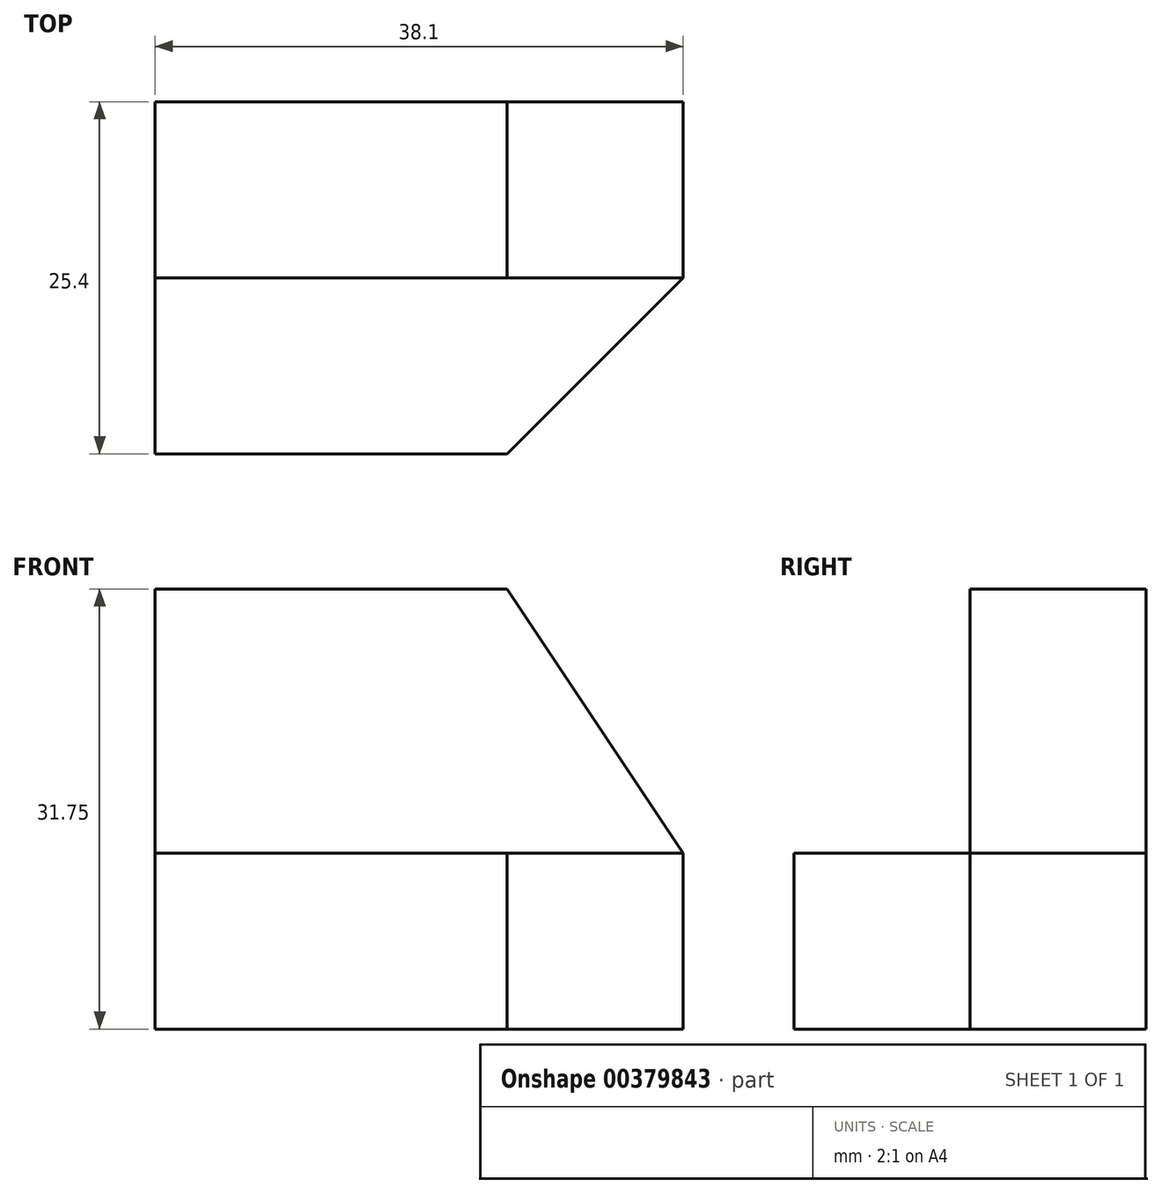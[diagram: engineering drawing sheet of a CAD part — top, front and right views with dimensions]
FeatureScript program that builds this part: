
annotation { "Feature Type Name" : "Feature", "Feature Type Description" : "" }
export const myFeature = defineFeature(function(context is Context, id is Id, definition is map)
    precondition{}
    {
        {
            var Q0;
            Q0=qCreatedBy(makeId("Front.planeOp"),FACE);
            var sketch = newSketch(context, id + "F0", { "sketchPlane" : qUnion([Q0])});
            skLineSegment(sketch, "E0", {"start": v(0, 0) * mm, "end": v(38.1, 0) * mm});
            skLineSegment(sketch, "E1", {"start": v(38.1, 0) * mm, "end": v(38.1, 31.75) * mm});
            skLineSegment(sketch, "E2", {"start": v(38.1, 31.75) * mm, "end": v(0, 31.75) * mm});
            skLineSegment(sketch, "E3", {"start": v(0, 31.75) * mm, "end": v(0, 0) * mm});
            skSolve(sketch);
        }
        {
            var Q0;
            Q0=makeQuery(id+"F0.imprint","IMPRINT",FACE,{"disambiguationData":[TD([[makeQuery(id+"F0.imprint","IMPRINT",EDGE,{"derivedFrom":sQuery(id+"F0.wireOp",EDGE,"E0")}),1.0]])]});
            extrude(context, id + "F1", {"entities" : qUnion([Q0]), "depth" : 25.4 * mm});
        }
        {
            var Q0;
            Q0=makeQuery(id+"F1.opExtrude","CAP_FACE",FACE,{"disambiguationData":[OSD([sQuery(id+"F0.wireOp",EDGE,"E0"),sQuery(id+"F0.wireOp",EDGE,"E1"),sQuery(id+"F0.wireOp",EDGE,"E2"),sQuery(id+"F0.wireOp",EDGE,"E3")])],"isStart":false});
            var sketch = newSketch(context, id + "F2", { "sketchPlane" : qUnion([Q0])});
            skLineSegment(sketch, "E4", {"start": v(0, 12.7) * mm, "end": v(38.1, 12.7) * mm});
            skSolve(sketch);
        }
        {
            var Q0;
            {var subQ0=sQuery(id+"F2.wireOp",EDGE,"E4");Q0=makeQuery(id+"F2.imprint","IMPRINT",FACE,{"disambiguationData":[TD([[makeQuery(id+"F2.imprint","IMPRINT",EDGE,{"derivedFrom":subQ0}),1.0]])]});}
            extrude(context, id + "F3", {"entities" : qUnion([Q0]), "operationType" : NewBodyOperationType.REMOVE, "oppositeDirection" : true, "depth" : 12.7 * mm});
        }
        {
            var Q0;
            Q0=makeQuery(id+"F3.boolean.opBoolean","COPY",FACE,{"derivedFrom":makeQuery(id+"F3.opExtrude","SWEPT_FACE",FACE,{"disambiguationData":[OSD([sQuery(id+"F2.wireOp",EDGE,"E4")])]})});
            var sketch = newSketch(context, id + "F4", { "sketchPlane" : qUnion([Q0])});
            skLineSegment(sketch, "E5", {"start": v(38.1, -12.7) * mm, "end": v(25.4, -25.4) * mm});
            skSolve(sketch);
        }
        {
            var Q0;
            {var subQ0=sQuery(id+"F4.wireOp",EDGE,"E5");Q0=makeQuery(id+"F4.imprint","IMPRINT",FACE,{"disambiguationData":[TD([[makeQuery(id+"F4.imprint","IMPRINT",EDGE,{"derivedFrom":subQ0}),1.0]])]});}
            extrude(context, id + "F5", {"entities" : qUnion([Q0]), "operationType" : NewBodyOperationType.REMOVE, "oppositeDirection" : true, "depth" : 12.7 * mm});
        }
        {
            var Q0;
            Q0=makeQuery(id+"F3.boolean.opBoolean","COPY",FACE,{"derivedFrom":makeQuery(id+"F3.opExtrude","CAP_FACE",FACE,{"disambiguationData":[OSD([sQuery(id+"F0.wireOp",EDGE,"E1"),sQuery(id+"F0.wireOp",EDGE,"E2"),sQuery(id+"F0.wireOp",EDGE,"E3"),sQuery(id+"F2.wireOp",EDGE,"E4")])],"isStart":false})});
            var sketch = newSketch(context, id + "F6", { "sketchPlane" : qUnion([Q0])});
            skLineSegment(sketch, "E6", {"start": v(38.1, 12.7) * mm, "end": v(25.4, 31.75) * mm});
            skSolve(sketch);
        }
        {
            var Q0;
            {var subQ0=sQuery(id+"F6.wireOp",EDGE,"E6");Q0=makeQuery(id+"F6.imprint","IMPRINT",FACE,{"disambiguationData":[TD([[makeQuery(id+"F6.imprint","IMPRINT",EDGE,{"derivedFrom":subQ0}),-1.0]])]});}
            var sketch = newSketch(context, id + "F7", { "sketchPlane" : qUnion([Q0])});
            skSolve(sketch);
        }
        {
            var Q0;
            Q0=qSketchRegion(id+"F7",true);
            var Q1;
            {var subQ0=sQuery(id+"F6.wireOp",EDGE,"E6");Q1=makeQuery(id+"F6.imprint","IMPRINT",FACE,{"disambiguationData":[TD([[makeQuery(id+"F6.imprint","IMPRINT",EDGE,{"derivedFrom":subQ0}),-1.0]])]});}
            extrude(context, id + "F8", {"entities" : qUnion([Q0, Q1]), "operationType" : NewBodyOperationType.REMOVE, "oppositeDirection" : true, "depth" : 25.4 * mm});
        }
    });
